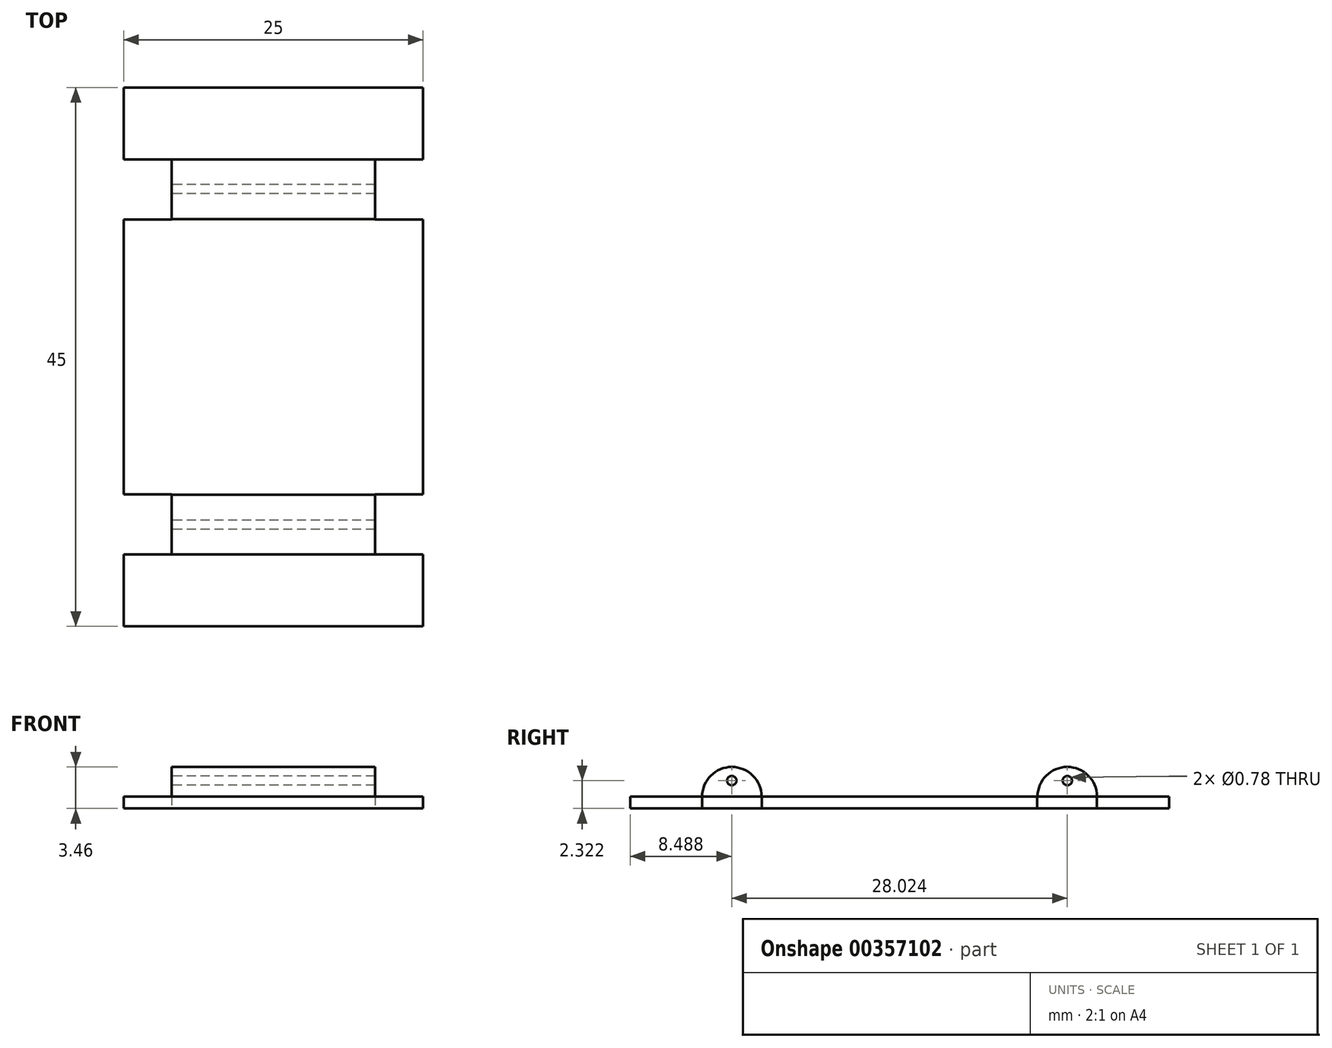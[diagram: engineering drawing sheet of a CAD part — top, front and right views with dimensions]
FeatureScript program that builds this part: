
annotation { "Feature Type Name" : "Feature", "Feature Type Description" : "" }
export const myFeature = defineFeature(function(context is Context, id is Id, definition is map)
    precondition{}
    {
        {
            var Q0;
            Q0=qCreatedBy(makeId("Top.planeOp"),FACE);
            var sketch = newSketch(context, id + "F0", { "sketchPlane" : qUnion([Q0])});
            skLineSegment(sketch, "E0.bottom", {"start": v(10.5, 22.5) * mm, "end": v(-10.5, 22.5) * mm});
            skLineSegment(sketch, "E0.top", {"start": v(12.5, -22.5) * mm, "end": v(-12.5, -22.5) * mm});
            skLineSegment(sketch, "E0.left", {"start": v(12.5, 20.5) * mm, "end": v(12.5, 16.49) * mm});
            skLineSegment(sketch, "E0.right", {"start": v(-12.5, 20.5) * mm, "end": v(-12.5, 16.49) * mm});
            skPoint(sketch, "E0.middle", {"position": v(0, 0) * mm});
            skLineSegment(sketch, "E1.bottom", {"start": v(-12.5, 16.49) * mm, "end": v(-8.5, 16.49) * mm});
            skLineSegment(sketch, "E1.top", {"start": v(-12.5, 11.49) * mm, "end": v(-8.5, 11.49) * mm});
            skLineSegment(sketch, "E1.right", {"start": v(-8.5, 16.49) * mm, "end": v(-8.5, 11.49) * mm});
            skLineSegment(sketch, "E2.MirrorCS", {"start": v(12.5, 16.49) * mm, "end": v(8.5, 16.49) * mm});
            skLineSegment(sketch, "E3.MirrorCS", {"start": v(8.5, 16.49) * mm, "end": v(8.5, 11.49) * mm});
            skLineSegment(sketch, "E4.MirrorCS", {"start": v(12.5, 11.49) * mm, "end": v(8.5, 11.49) * mm});
            skLineSegment(sketch, "E5.MirrorCS", {"start": v(-12.5, -11.49) * mm, "end": v(-8.5, -11.49) * mm});
            skLineSegment(sketch, "E6.MirrorCS", {"start": v(-8.5, -16.49) * mm, "end": v(-8.5, -11.49) * mm});
            skLineSegment(sketch, "E7.MirrorCS", {"start": v(-12.5, -16.49) * mm, "end": v(-8.5, -16.49) * mm});
            skLineSegment(sketch, "E8.MirrorCS", {"start": v(12.5, -11.49) * mm, "end": v(8.5, -11.49) * mm});
            skLineSegment(sketch, "E9.MirrorCS", {"start": v(8.5, -16.49) * mm, "end": v(8.5, -11.49) * mm});
            skLineSegment(sketch, "E10.MirrorCS", {"start": v(12.5, -16.49) * mm, "end": v(8.5, -16.49) * mm});
            skLineSegment(sketch, "E11.trimOffspring", {"start": v(12.5, 11.49) * mm, "end": v(12.5, -11.49) * mm});
            skLineSegment(sketch, "E12.trimOffspring", {"start": v(-12.5, 11.49) * mm, "end": v(-12.5, -11.49) * mm});
            skLineSegment(sketch, "E13.trimOffspring", {"start": v(-12.5, -16.49) * mm, "end": v(-12.5, -22.5) * mm});
            skLineSegment(sketch, "E14.trimOffspring", {"start": v(12.5, -16.49) * mm, "end": v(12.5, -22.5) * mm});
            skPoint(sketch, "E15.visualSharp", {"position": v(-12.5, 22.5) * mm});
            skPoint(sketch, "E16.visualSharp", {"position": v(12.5, 22.5) * mm});
            skLineSegment(sketch, "E17", {"start": v(-12.5, 20.5) * mm, "end": v(-12.5, 22.5) * mm});
            skLineSegment(sketch, "E18", {"start": v(-12.5, 22.5) * mm, "end": v(-10.5, 22.5) * mm});
            skLineSegment(sketch, "E19", {"start": v(10.5, 22.5) * mm, "end": v(12.5, 22.5) * mm});
            skLineSegment(sketch, "E20", {"start": v(12.5, 20.5) * mm, "end": v(12.5, 22.5) * mm});
            skSolve(sketch);
        }
        {
            var Q0;
            Q0 = qSketchRegion(id + "F0", true);
            extrude(context, id + "F1", {"entities" : qUnion([Q0]), "depth" : 1 * mm});
        }
        {
            var Q0;
            Q0=qCreatedBy(makeId("Right.planeOp"),FACE);
            var sketch = newSketch(context, id + "F2", { "sketchPlane" : qUnion([Q0])});
            skArc(sketch, "E21", {"start": v(-11.52, 1) * mm, "mid": v(-14, 3.46) * mm, "end": v(-16.48, 1) * mm});
            skLineSegment(sketch, "E22", {"start": v(-16.48, 1) * mm, "end": v(-11.52, 1) * mm});
            skCircle(sketch, "E23", {"center": v(-14.01, 2.32) * mm, "radius": 0.39 * mm});
            skArc(sketch, "E24.MirrorCS", {"start": v(11.52, 1) * mm, "mid": v(14, 3.46) * mm, "end": v(16.48, 1) * mm});
            skCircle(sketch, "E25.MirrorC", {"center": v(14.01, 2.32) * mm, "radius": 0.39 * mm});
            skLineSegment(sketch, "E26.MirrorCS", {"start": v(16.48, 1) * mm, "end": v(11.52, 1) * mm});
            skSolve(sketch);
        }
        {
            var Q0;
            Q0 = qSketchRegion(id + "F2", true);
            extrude(context, id + "F3", {"entities" : qUnion([Q0]), "operationType" : NewBodyOperationType.ADD, "endBound" : BoundingType.SYMMETRIC, "depth" : 16.96 * mm});
        }
    });
